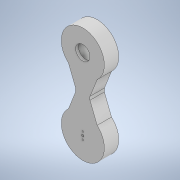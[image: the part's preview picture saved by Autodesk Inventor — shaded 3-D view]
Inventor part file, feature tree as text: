
AUTODESK INVENTOR PART (.ipt)
format: ipt  version: 2022 (Build 260153000, 153)  size: 240,640 bytes
history: native  units: in
note: dims shown in document units (in); Inventor stores cm internally (conversion verified against a paired STEP export)
features: extrude x12, sketch x12, thread x4, chamfer x1
ambient origin geometry x8: Origin, YZ Plane, XZ Plane, XY Plane, X Axis, Y Axis, Z Axis, Center Point
bodies: Solid1 (feature_tree)
feature tree (29):
  extrude  "Extrusion1"  Depth=2.3622in
  extrude  "Extrusion2"  Depth=0.7874in TaperAngle=0.0deg
  extrude  "Extrusion3"  Depth=0.6299in TaperAngle=0.0deg
  extrude  "Extrusion4"  Depth=0.0787in
  extrude  "Extrusion5"  Depth=0.0787in TaperAngle=0.0deg
  extrude  "Extrusion6"  Depth=1.1811in
  extrude  "Extrusion7"  Depth=0.3937in
  extrude  "Extrusion8"  Depth=0.2992in
  extrude  "Extrusion9"  Depth=0.2992in
  extrude  "Extrusion10"  Depth=0.1969in
  extrude  "Extrusion11"  Depth=0.1969in
  chamfer  "Chamfer2"  Distance=0.3937in
  thread  "Thread5"  [1 undecoded]
  thread  "Thread6"  [1 undecoded]
  thread  "Thread7"  [1 undecoded]
  thread  "Thread8"  [1 undecoded]
  extrude  "Extrusion12"  Depth=0.3937in
  sketch  "Sketch1"  dims[d0=2.3622in d1=2.3622in]
  sketch  "Sketch2"  dims[d2=1.5748in d3=0.7874in d4=0.0in]
  sketch  "Sketch3"  dims[d5=0.7874in d6=0.6299in d7=0.0in]
  sketch  "Sketch4"  dims[d11=0.0787in d12=0.0787in]
  sketch  "Sketch5"  dims[d13=0.0787in d14=1.1201in d15=0.0in]
  sketch  "Sketch6"  dims[d16=0.3937in d17=1.1811in]
  sketch  "Sketch7"  dims[d18=0.3937in d19=0.4134in]
  sketch  "Sketch8"  dims[d20=0.6299in d21=0.0in d22=0.2992in]
  sketch  "Sketch9"  dims[d23=0.2992in d24=0.1614in]
  sketch  "Sketch10"  dims[d25=0.1614in d26=0.1969in]
  sketch  "Sketch11"  dims[d27=0.1969in d28=0.1969in]
  sketch  "Sketch12"  dims[d29=0.1969in d30=0.3937in d31=0.0in d32=0.1614in d33=0.1614in d34=0.1969in d35=0.1969in d36=0.1063in d37=0.1063in d38=0.1063in d39=0.1063in d40=0.315in d41=0.0in d50=0.7874in d51=0.1575in d52=0.0in d53=0.7874in d54=1.1811in d55=1.1811in d56=2.8425in d57=0.0in d58=0.7874in d59=0.0in d60=0.7874in d61=0.6299in d62=0.0in d63=0.0787in d64=0.0787in d65=0.8701in d66=0.0in d67=0.4724in d68=0.0787in d69=45.0deg d70=0.315in d71=0.0in d72=0.315in d73=0.0in d74=0.315in d75=0.0in d76=0.315in d77=0.0in d78=0.1181in d79=0.3937in d80=0.0in d42=0.0197in d43=0.0344in]
note: 4 required parameter values undecoded (feature->parameter linkage not recoverable at this tier; creation-order binding heuristic only, values carry confidence <= 0.55)
